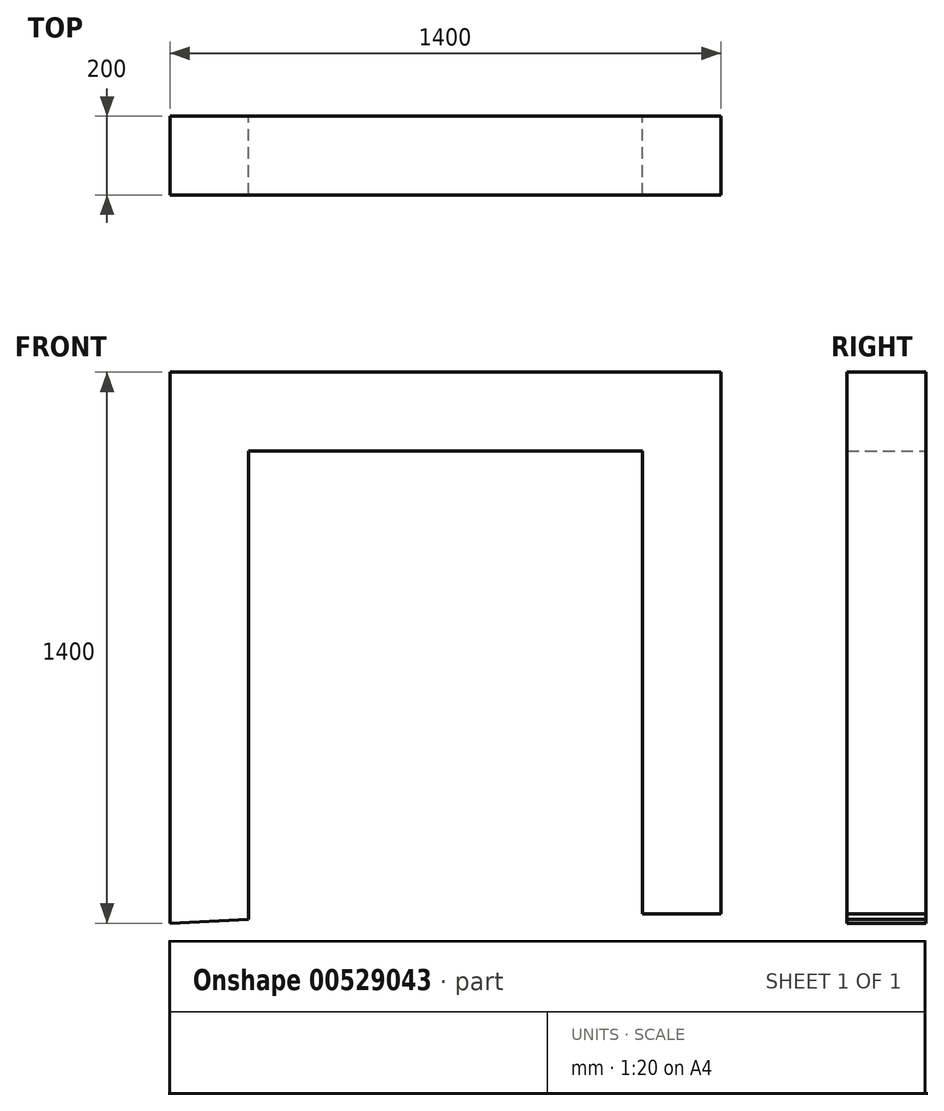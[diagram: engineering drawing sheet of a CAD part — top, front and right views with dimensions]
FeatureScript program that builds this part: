
annotation { "Feature Type Name" : "Feature", "Feature Type Description" : "" }
export const myFeature = defineFeature(function(context is Context, id is Id, definition is map)
    precondition{}
    {
        {
            var Q0;
            Q0=qCreatedBy(makeId("Front.planeOp"),FACE);
            var sketch = newSketch(context, id + "F0", { "sketchPlane" : qUnion([Q0])});
            skLineSegment(sketch, "E0", {"start": v(-794.51, -714.56) * mm, "end": v(-794.51, 685.44) * mm});
            skLineSegment(sketch, "E1", {"start": v(-794.51, 685.44) * mm, "end": v(605.49, 685.44) * mm});
            skLineSegment(sketch, "E2", {"start": v(605.49, 685.44) * mm, "end": v(605.49, -690.75) * mm});
            skLineSegment(sketch, "E3", {"start": v(605.49, -690.75) * mm, "end": v(405.49, -690.75) * mm});
            skLineSegment(sketch, "E4", {"start": v(405.49, -690.75) * mm, "end": v(405.49, 485.44) * mm});
            skLineSegment(sketch, "E5", {"start": v(405.49, 485.44) * mm, "end": v(-594.51, 485.44) * mm});
            skLineSegment(sketch, "E6", {"start": v(-594.51, 485.44) * mm, "end": v(-594.51, -705.03) * mm});
            skLineSegment(sketch, "E7", {"start": v(-594.51, -705.03) * mm, "end": v(-794.51, -714.56) * mm});
            skSolve(sketch);
        }
        {
            var Q0;
            Q0=makeQuery(id+"F0.imprint","IMPRINT",FACE,{"disambiguationData":[TD([[makeQuery(id+"F0.imprint","IMPRINT",EDGE,{"derivedFrom":sQuery(id+"F0.wireOp",EDGE,"E0")}),-1.0]])]});
            extrude(context, id + "F1", {"entities" : qUnion([Q0]), "depth" : 200 * mm, "offsetDistance" : 25 * mm});
        }
    });
